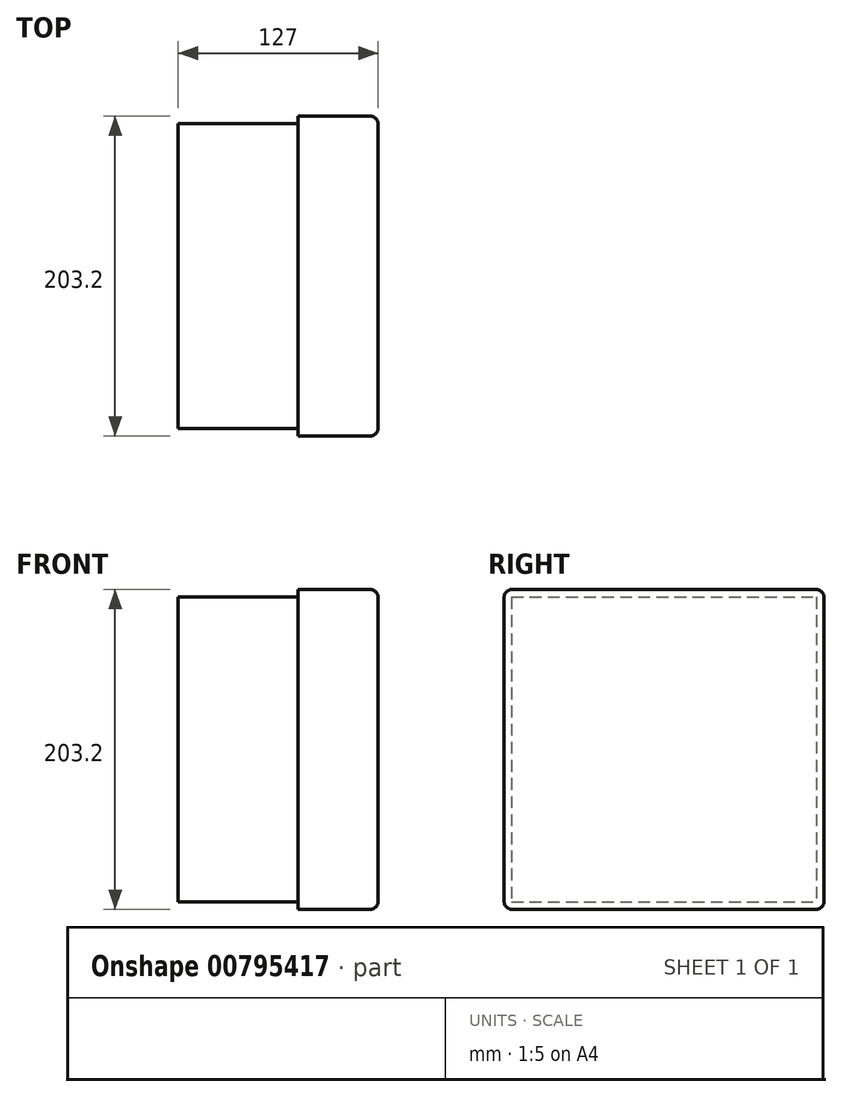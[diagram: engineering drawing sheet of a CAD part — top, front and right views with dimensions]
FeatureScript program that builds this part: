
annotation { "Feature Type Name" : "Feature", "Feature Type Description" : "" }
export const myFeature = defineFeature(function(context is Context, id is Id, definition is map)
    precondition{}
    {
        {
            var Q0;
            Q0=qCreatedBy(makeId("Right.planeOp"),FACE);
            var sketch = newSketch(context, id + "F0", { "sketchPlane" : qUnion([Q0])});
            skLineSegment(sketch, "E0.bottom", {"start": v(101.6, 101.6) * mm, "end": v(-101.6, 101.6) * mm});
            skLineSegment(sketch, "E0.top", {"start": v(101.6, -101.6) * mm, "end": v(-101.6, -101.6) * mm});
            skLineSegment(sketch, "E0.left", {"start": v(101.6, 101.6) * mm, "end": v(101.6, -101.6) * mm});
            skLineSegment(sketch, "E0.right", {"start": v(-101.6, 101.6) * mm, "end": v(-101.6, -101.6) * mm});
            skPoint(sketch, "E0.middle", {"position": v(0, 0) * mm});
            skSolve(sketch);
        }
        {
            var Q0;
            Q0 = qSketchRegion(id + "F0", true);
            extrude(context, id + "F1", {"entities" : qUnion([Q0]), "depth" : 127 * mm, "offsetDistance" : 25.4 * mm});
        }
        {
            var Q0;
            Q0=makeQuery(id+"F1.opExtrude","CAP_FACE",FACE,{"disambiguationData":[OSD([sQuery(id+"F0.wireOp",EDGE,"E0.bottom"),sQuery(id+"F0.wireOp",EDGE,"E0.top"),sQuery(id+"F0.wireOp",EDGE,"E0.left"),sQuery(id+"F0.wireOp",EDGE,"E0.right")])],"isStart":true});
            var sketch = newSketch(context, id + "F2", { "sketchPlane" : qUnion([Q0])});
            skLineSegment(sketch, "E1.bottom", {"start": v(96.84, 96.84) * mm, "end": v(-96.84, 96.84) * mm});
            skLineSegment(sketch, "E1.top", {"start": v(96.84, -96.84) * mm, "end": v(-96.84, -96.84) * mm});
            skLineSegment(sketch, "E1.left", {"start": v(96.84, 96.84) * mm, "end": v(96.84, -96.84) * mm});
            skLineSegment(sketch, "E1.right", {"start": v(-96.84, 96.84) * mm, "end": v(-96.84, -96.84) * mm});
            skPoint(sketch, "E1.middle", {"position": v(0, 0) * mm});
            skSolve(sketch);
        }
        {
            var Q0;
            Q0=makeQuery(id+"F2.imprint","IMPRINT",FACE,{"disambiguationData":[TD([[makeQuery(id+"F2.imprint","IMPRINT",EDGE,{"derivedFrom":sQuery(id+"F2.wireOp",EDGE,"E1.bottom")}),-1.0]])]});
            extrude(context, id + "F3", {"entities" : qUnion([Q0]), "operationType" : NewBodyOperationType.REMOVE, "oppositeDirection" : true, "depth" : 76.2 * mm, "offsetDistance" : 25.4 * mm});
        }
        {
            var Q0;
            Q0=makeQuery(id+"F1.opExtrude","SWEPT_EDGE",EDGE,{"disambiguationData":[OSD([sQuery(id+"F0.wireOp",EDGE,"E0.bottom"),sQuery(id+"F0.wireOp",EDGE,"E0.left")])]});
            var Q1;
            Q1=makeQuery(id+"F1.opExtrude","CAP_EDGE",EDGE,{"disambiguationData":[OSD([sQuery(id+"F0.wireOp",EDGE,"E0.left")])],"isStart":false});
            var Q2;
            Q2=makeQuery(id+"F1.opExtrude","SWEPT_EDGE",EDGE,{"disambiguationData":[OSD([sQuery(id+"F0.wireOp",EDGE,"E0.top"),sQuery(id+"F0.wireOp",EDGE,"E0.left")])]});
            var Q3;
            Q3=makeQuery(id+"F1.opExtrude","CAP_EDGE",EDGE,{"disambiguationData":[OSD([sQuery(id+"F0.wireOp",EDGE,"E0.top")])],"isStart":false});
            var Q4;
            Q4=makeQuery(id+"F1.opExtrude","CAP_EDGE",EDGE,{"disambiguationData":[OSD([sQuery(id+"F0.wireOp",EDGE,"E0.bottom")])],"isStart":false});
            var Q5;
            Q5=makeQuery(id+"F1.opExtrude","CAP_EDGE",EDGE,{"disambiguationData":[OSD([sQuery(id+"F0.wireOp",EDGE,"E0.right")])],"isStart":false});
            var Q6;
            Q6=makeQuery(id+"F1.opExtrude","SWEPT_EDGE",EDGE,{"disambiguationData":[OSD([sQuery(id+"F0.wireOp",EDGE,"E0.bottom"),sQuery(id+"F0.wireOp",EDGE,"E0.right")])]});
            var Q7;
            Q7=makeQuery(id+"F1.opExtrude","SWEPT_EDGE",EDGE,{"disambiguationData":[OSD([sQuery(id+"F0.wireOp",EDGE,"E0.top"),sQuery(id+"F0.wireOp",EDGE,"E0.right")])]});
            fillet(context, id + "F4", {"entities" : qUnion([Q0, Q1, Q2, Q3, Q4, Q5, Q6, Q7]), "tangentPropagation" : true, "radius" : 5.08 * mm, "defaultsChanged" : false, "vertexSettings" : [], "allowEdgeOverflow" : false});
        }
    });
